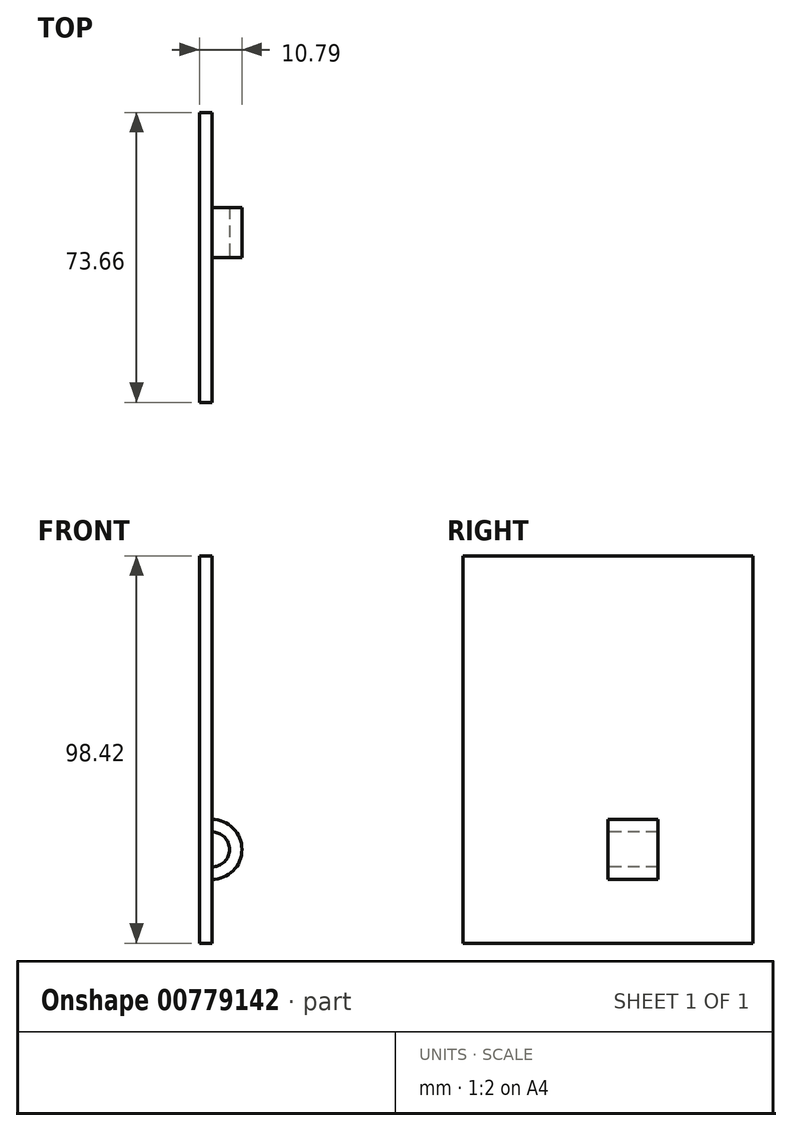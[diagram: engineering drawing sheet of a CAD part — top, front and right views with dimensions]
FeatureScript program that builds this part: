
annotation { "Feature Type Name" : "Feature", "Feature Type Description" : "" }
export const myFeature = defineFeature(function(context is Context, id is Id, definition is map)
    precondition{}
    {
        {
            var Q0;
            Q0=qCreatedBy(makeId("Right.planeOp"),FACE);
            var sketch = newSketch(context, id + "F0", { "sketchPlane" : qUnion([Q0])});
            skLineSegment(sketch, "E0.bottom", {"start": v(36.83, 49.21) * mm, "end": v(-36.83, 49.21) * mm});
            skLineSegment(sketch, "E0.top", {"start": v(36.83, -49.21) * mm, "end": v(-36.83, -49.21) * mm});
            skLineSegment(sketch, "E0.left", {"start": v(36.83, 49.21) * mm, "end": v(36.83, -49.21) * mm});
            skLineSegment(sketch, "E0.right", {"start": v(-36.83, 49.21) * mm, "end": v(-36.83, -49.21) * mm});
            skPoint(sketch, "E0.middle", {"position": v(0, 0) * mm});
            skSolve(sketch);
        }
        {
            var Q0;
            Q0 = qSketchRegion(id + "F0", true);
            extrude(context, id + "F1", {"entities" : qUnion([Q0]), "oppositeDirection" : true, "depth" : 3.17 * mm, "offsetDistance" : 25.4 * mm});
        }
        {
            var Q0;
            Q0=qCreatedBy(makeId("Front.planeOp"),FACE);
            var sketch = newSketch(context, id + "F2", { "sketchPlane" : qUnion([Q0])});
            skArc(sketch, "E1", {"start": v(0, -33.02) * mm, "mid": v(7.62, -25.4) * mm, "end": v(0, -17.78) * mm});
            skArc(sketch, "E2", {"start": v(0, -29.85) * mm, "mid": v(4.44, -25.4) * mm, "end": v(0, -20.96) * mm});
            skLineSegment(sketch, "E3", {"start": v(0, -17.78) * mm, "end": v(0, -20.96) * mm});
            skLineSegment(sketch, "E4", {"start": v(0, -29.85) * mm, "end": v(0, -33.02) * mm});
            skSolve(sketch);
        }
        {
            var Q0;
            Q0=makeQuery(id+"F2.imprint","IMPRINT",FACE,{"disambiguationData":[TD([[makeQuery(id+"F2.imprint","IMPRINT",EDGE,{"derivedFrom":sQuery(id+"F2.wireOp",EDGE,"E1")}),1.0]])]});
            extrude(context, id + "F3", {"entities" : qUnion([Q0]), "operationType" : NewBodyOperationType.ADD, "oppositeDirection" : true, "depth" : 12.7 * mm, "offsetDistance" : 25.4 * mm});
        }
    });
